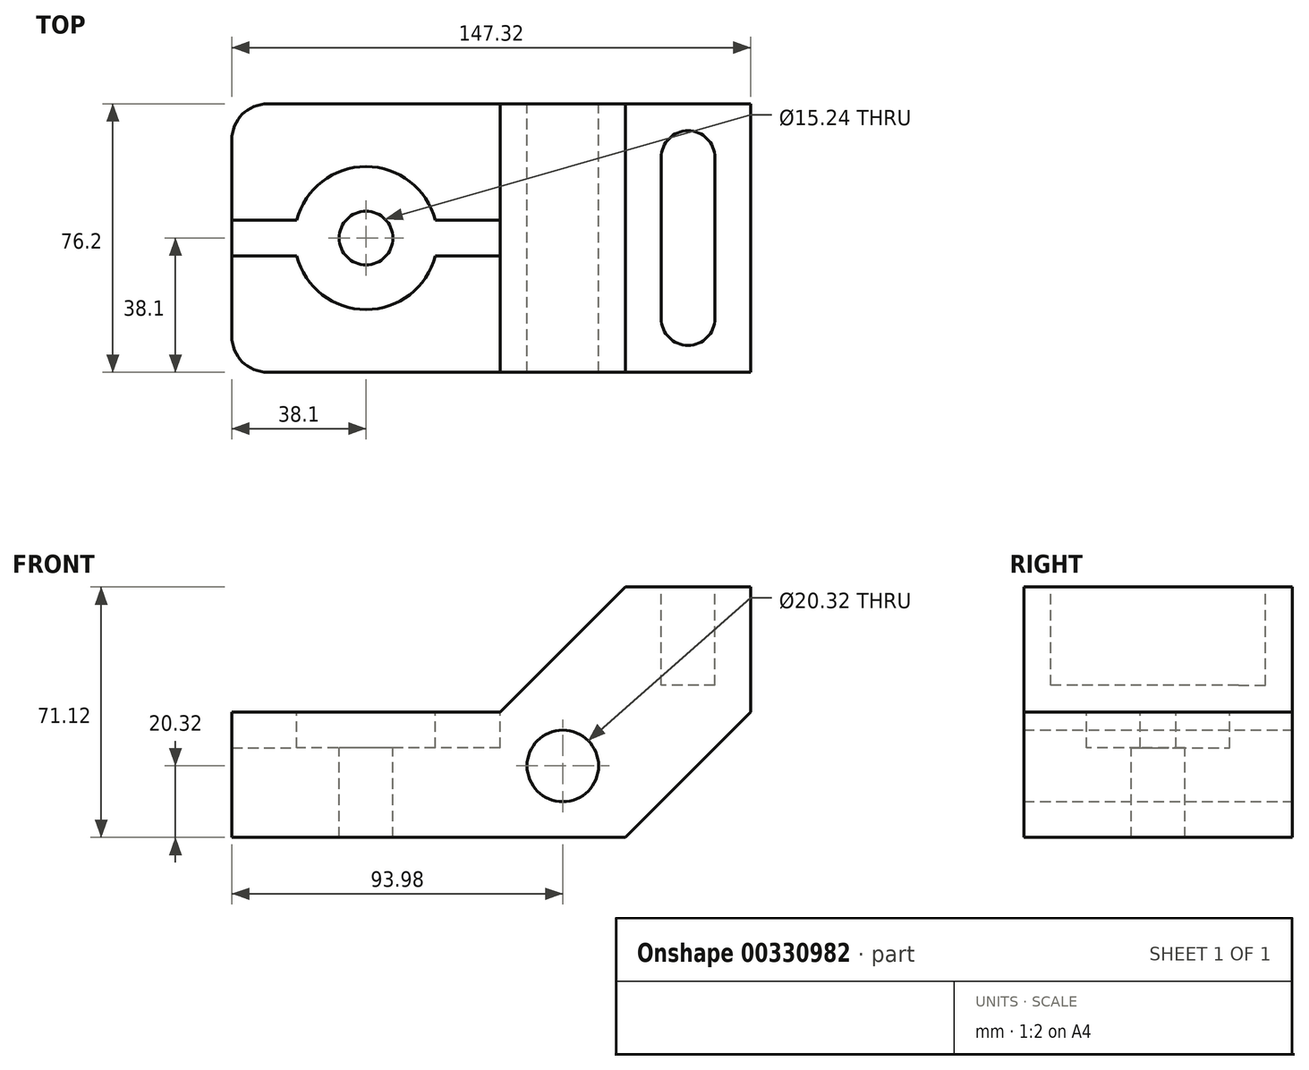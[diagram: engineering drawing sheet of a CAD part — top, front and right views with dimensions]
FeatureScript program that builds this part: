
annotation { "Feature Type Name" : "Feature", "Feature Type Description" : "" }
export const myFeature = defineFeature(function(context is Context, id is Id, definition is map)
    precondition{}
    {
        {
            var Q0;
            Q0=qCreatedBy(makeId("Front.planeOp"),FACE);
            var sketch = newSketch(context, id + "F0", { "sketchPlane" : qUnion([Q0])});
            skLineSegment(sketch, "E0", {"start": v(0, 0) * mm, "end": v(111.76, 0) * mm});
            skLineSegment(sketch, "E1", {"start": v(111.76, 0) * mm, "end": v(147.32, 35.56) * mm});
            skLineSegment(sketch, "E2", {"start": v(147.32, 35.56) * mm, "end": v(147.32, 71.12) * mm});
            skLineSegment(sketch, "E3", {"start": v(147.32, 71.12) * mm, "end": v(111.76, 71.12) * mm});
            skLineSegment(sketch, "E4", {"start": v(111.76, 71.12) * mm, "end": v(76.2, 35.56) * mm});
            skLineSegment(sketch, "E5", {"start": v(76.2, 35.56) * mm, "end": v(0, 35.56) * mm});
            skLineSegment(sketch, "E6", {"start": v(0, 35.56) * mm, "end": v(0, 0) * mm});
            skCircle(sketch, "E7", {"center": v(93.98, 20.32) * mm, "radius": 10.16 * mm});
            skSolve(sketch);
        }
        {
            var Q0;
            Q0 = qSketchRegion(id + "F0", true);
            extrude(context, id + "F1", {"entities" : qUnion([Q0]), "depth" : 76.2 * mm});
        }
        {
            var Q0;
            Q0=makeQuery(id+"F1.opExtrude","SWEPT_FACE",FACE,{"disambiguationData":[OSD([sQuery(id+"F0.wireOp",EDGE,"E3")])]});
            var sketch = newSketch(context, id + "F2", { "sketchPlane" : qUnion([Q0])});
            skLineSegment(sketch, "E8", {"start": v(129.54, -15.24) * mm, "end": v(129.54, -60.96) * mm, "construction": true});
            skPoint(sketch, "E8.startSnap0", {"position": v(129.54, 0) * mm});
            skPoint(sketch, "E8.endSnap0", {"position": v(129.54, -76.2) * mm});
            skArc(sketch, "E9.0.startCap", {"start": v(121.92, -15.24) * mm, "mid": v(129.54, -7.62) * mm, "end": v(137.16, -15.24) * mm});
            skArc(sketch, "E9.0.endCap", {"start": v(137.16, -60.96) * mm, "mid": v(129.54, -68.58) * mm, "end": v(121.92, -60.96) * mm});
            skLineSegment(sketch, "E9.0.left", {"start": v(137.16, -15.24) * mm, "end": v(137.16, -60.96) * mm});
            skLineSegment(sketch, "E9.0.right", {"start": v(121.92, -15.24) * mm, "end": v(121.92, -60.96) * mm});
            skSolve(sketch);
        }
        {
            var Q0;
            Q0 = qSketchRegion(id + "F2", true);
            extrude(context, id + "F3", {"entities" : qUnion([Q0]), "operationType" : NewBodyOperationType.REMOVE, "oppositeDirection" : true, "depth" : 27.94 * mm});
        }
        {
            var Q0;
            Q0=makeQuery(id+"F1.opExtrude","SWEPT_FACE",FACE,{"disambiguationData":[OSD([sQuery(id+"F0.wireOp",EDGE,"E5")])]});
            var sketch = newSketch(context, id + "F4", { "sketchPlane" : qUnion([Q0])});
            skLineSegment(sketch, "E10", {"start": v(0, -33.02) * mm, "end": v(76.2, -33.02) * mm});
            skLineSegment(sketch, "E11", {"start": v(76.2, -33.02) * mm, "end": v(76.2, -43.18) * mm});
            skLineSegment(sketch, "E12", {"start": v(76.2, -43.18) * mm, "end": v(0, -43.18) * mm});
            skLineSegment(sketch, "E13", {"start": v(0, -43.18) * mm, "end": v(0, -33.02) * mm});
            skLineSegment(sketch, "E14", {"start": v(76.2, -38.1) * mm, "end": v(-18, -38.1) * mm, "construction": true});
            skPoint(sketch, "E14.endSnap0", {"position": v(76.2, -38.1) * mm});
            skLineSegment(sketch, "E15", {"start": v(38.1, 0) * mm, "end": v(38.1, -76.2) * mm, "construction": true});
            skSolve(sketch);
        }
        {
            var Q0;
            {var subQ0=sQuery(id+"F4.wireOp",EDGE,"E10");Q0=makeQuery(id+"F4.imprint","IMPRINT",FACE,{"disambiguationData":[TD([[makeQuery(id+"F4.imprint","IMPRINT",EDGE,{"derivedFrom":subQ0}),1.0]])]});}
            var sketch = newSketch(context, id + "F5", { "sketchPlane" : qUnion([Q0])});
            skPoint(sketch, "E16.0", {"position": v(38.1, -38.1) * mm});
            skSolve(sketch);
        }
        {
            var Q0;
            Q0=sQuery(id+"F5.wireOp",VERTEX,"E16.0");
            var Q1;
            Q1=makeQuery(id+"F1.opExtrude","SWEPT_BODY",BODY,{"disambiguationData":[OSD([sQuery(id+"F0.wireOp",EDGE,"E0"),sQuery(id+"F0.wireOp",EDGE,"E1"),sQuery(id+"F0.wireOp",EDGE,"E2"),sQuery(id+"F0.wireOp",EDGE,"E3"),sQuery(id+"F0.wireOp",EDGE,"E4"),sQuery(id+"F0.wireOp",EDGE,"E5"),sQuery(id+"F0.wireOp",EDGE,"E6"),sQuery(id+"F0.wireOp",EDGE,"E7")])]});
            hole(context, id + "F6", {"style" : HoleStyle.C_BORE, "endStyle" : HoleEndStyle.BLIND, "holeDiameter" : 15.24 * mm, "cBoreDiameter" : 40.64 * mm, "cBoreDepth" : 10.16 * mm, "holeDepth" : 35.56 * mm, "tappedDepth" : 12.7 * mm, "tapClearance" : 3, "startFromSketch" : true, "locations" : qUnion([Q0]), "scope" : qUnion([Q1])});
        }
        {
            var Q0;
            Q0=makeQuery(id+"F4.imprint","IMPRINT",FACE,{"disambiguationData":[TD([[makeQuery(id+"F4.imprint","IMPRINT",EDGE,{"derivedFrom":sQuery(id+"F4.wireOp",EDGE,"E10")}),-1.0]])]});
            extrude(context, id + "F7", {"entities" : qUnion([Q0]), "operationType" : NewBodyOperationType.REMOVE, "oppositeDirection" : true, "depth" : 10.16 * mm});
        }
        {
            var Q0;
            Q0=makeQuery(id+"F1.opExtrude","CAP_EDGE",EDGE,{"disambiguationData":[OSD([sQuery(id+"F0.wireOp",EDGE,"E6")])],"isStart":false});
            var Q1;
            Q1=makeQuery(id+"F1.opExtrude","CAP_EDGE",EDGE,{"disambiguationData":[OSD([sQuery(id+"F0.wireOp",EDGE,"E6")])],"isStart":true});
            fillet(context, id + "F8", {"entities" : qUnion([Q0, Q1]), "radius" : 10.16 * mm, "tangentPropagation" : true, "allowEdgeOverflow" : false});
        }
    });
